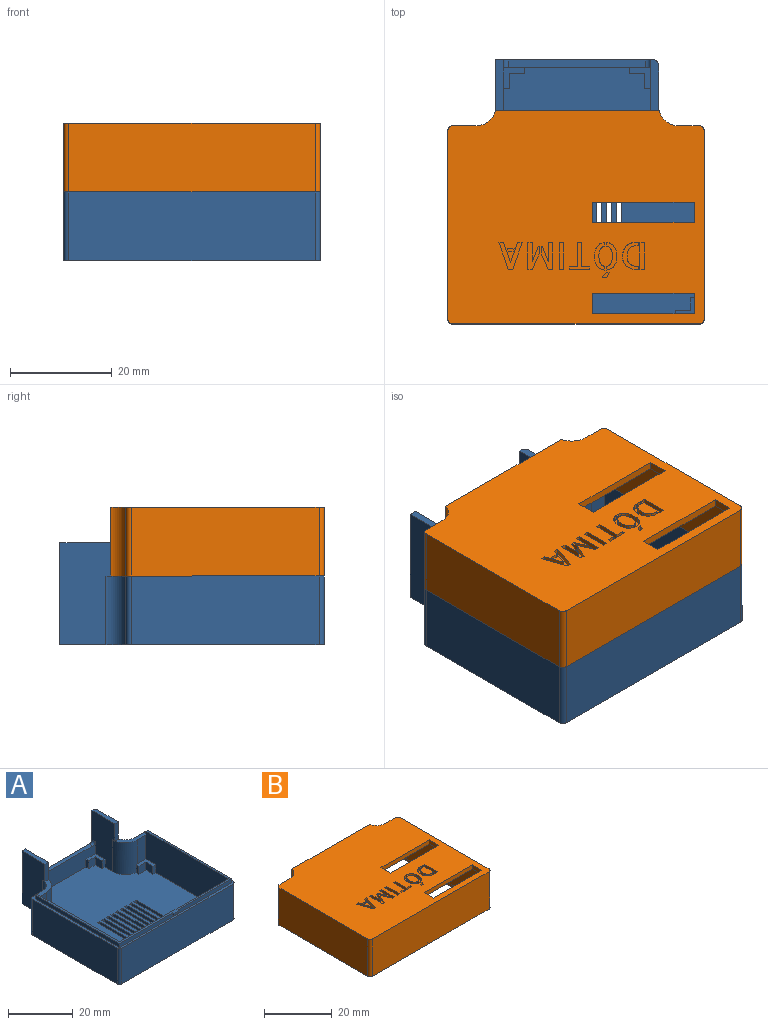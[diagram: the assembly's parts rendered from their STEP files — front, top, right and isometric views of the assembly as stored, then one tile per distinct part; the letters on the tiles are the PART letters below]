
ASSEMBLY  parts=2 mates=1
PART A: 116 faces, bbox 50.5x52x20 mm
  f0: plane 36.75x1.5mm, normal (-1,0,0), area 55.1mm2, adj f1,f5,f14,f115
  f1: plane 49x37.25mm, normal (0,0,1), area 92mm2, adj f0,f4,f5,f9,f25,f26,f110,f112
  f2: cylinder r=5.43mm len=12mm, axis (0,0,-1), area 99.1mm2, adj f7,f8,f11,f14,f66,f70,f101
  f3: cylinder r=5.43mm len=12mm, axis (0,0,-1), area 102.4mm2, adj f6,f8,f14,f27,f78,f98
  f4: plane 36.75x1.5mm, normal (1,0,0), area 55.1mm2, adj f1,f5,f14,f114
  f5: plane 49x1.5mm, normal (0,-1,0), area 71.6mm2, adj f0,f1,f4,f14,f110,f111,f112
  f6: plane 18.5x10mm, normal (-1,0,0), area 149.9mm2, adj f3,f8,f10,f15,f72,f75,f97,f98
  f7: plane 18.5x10mm, normal (1,0,0), area 149.9mm2, adj f2,f8,f10,f15,f92,f96,f100,f101
  f8: plane 49x47.5mm, normal (0,0,1), area 1907.6mm2, adj f2,f3,f6,f7,f9,f10,f25,f26
  f9: plane 36x13.5mm, normal (-1,0,0), area 462.3mm2, adj f1,f8,f26,f27,f77,f81,f83,f86
  f10: plane 29x7.5mm, normal (0,-1,0), area 163.7mm2, adj f6,f7,f8,f28,f73,f75,f95,f96
  f11: plane 12x4.07mm, normal (0,-1,0), area 41.3mm2, adj f2,f13,f14,f25,f65,f66
  f12: plane 52x50.5mm, normal (0,0,-1), area 2256.1mm2, adj f15,f16,f17,f18,f19,f20,f21,f22
  f13: plane 1.57x0.05mm, normal (0,0,1), area 0mm2, adj f11,f25,f65
  f14: plane 50.5x42.93mm, normal (0,0,1), area 127.4mm2, adj f0,f2,f3,f4,f5,f11,f16,f17
  f15: plane 31x20mm, normal (0,1,0), area 272.4mm2, adj f6,f7,f12,f21,f28,f99,f102,f103
  f16: plane 37x13.5mm, normal (1,0,0), area 499.5mm2, adj f12,f14,f108,f109
  f17: plane 48.5x13.5mm, normal (0,-1,0), area 654.8mm2, adj f12,f14,f107,f108
  f18: plane 37x13.5mm, normal (-1,0,0), area 499.5mm2, adj f12,f14,f106,f107
  f19: plane 13.5x4.57mm, normal (0,1,0), area 61.6mm2, adj f12,f14,f20,f106
  f20: cylinder r=3.93mm len=13.5mm, axis (0,0,-1), area 83.4mm2, adj f12,f14,f19,f21
  f21: plane 20x10mm, normal (-1,0,0), area 187.4mm2, adj f12,f14,f15,f20,f100,f102
  f22: plane 20x9mm, normal (1,0,0), area 167.4mm2, adj f12,f14,f23,f97,f99,f105
  f23: cylinder r=3.93mm len=13.5mm, axis (0,0,-1), area 83.4mm2, adj f12,f14,f22,f24
  f24: plane 13.5x4.07mm, normal (0,1,0), area 54.9mm2, adj f12,f14,f23,f109
  f25: plane 36x13.5mm, normal (1,0,0), area 445.9mm2, adj f1,f8,f11,f13,f26,f65,f66,f67
  f26: plane 47.5x13.5mm, normal (0,1,0), area 619mm2, adj f1,f8,f9,f25,f82,f86,f87,f91
  f27: plane 9x3.57mm, normal (0,-1,0), area 32.1mm2, adj f3,f9,f14,f81
  f28: plane 27x1.5mm, normal (0,0,1), area 40.5mm2, adj f10,f15,f103,f104
  f29: plane 15x1.5mm, normal (1,0,0), area 22.5mm2, adj f8,f12,f30,f32
  f30: plane 1.5x1mm, normal (0,-1,0), area 1.5mm2, adj f8,f12,f29,f31
  f31: plane 15x1.5mm, normal (-1,0,0), area 22.5mm2, adj f8,f12,f30,f32
  f32: plane 1.5x1mm, normal (0,1,0), area 1.5mm2, adj f8,f12,f29,f31
  f33: plane 1.5x1mm, normal (0,-1,0), area 1.5mm2, adj f8,f12,f34,f36
  f34: plane 15x1.5mm, normal (-1,0,0), area 22.5mm2, adj f8,f12,f33,f35
  f35: plane 1.5x1mm, normal (0,1,0), area 1.5mm2, adj f8,f12,f34,f36
  f36: plane 15x1.5mm, normal (1,0,0), area 22.5mm2, adj f8,f12,f33,f35
  f37: plane 1.5x1mm, normal (0,-1,0), area 1.5mm2, adj f8,f12,f38,f40
  f38: plane 15x1.5mm, normal (-1,0,0), area 22.5mm2, adj f8,f12,f37,f39
  f39: plane 1.5x1mm, normal (0,1,0), area 1.5mm2, adj f8,f12,f38,f40
  f40: plane 15x1.5mm, normal (1,0,0), area 22.5mm2, adj f8,f12,f37,f39
  f41: plane 1.5x1mm, normal (0,-1,0), area 1.5mm2, adj f8,f12,f42,f44
  f42: plane 15x1.5mm, normal (-1,0,0), area 22.5mm2, adj f8,f12,f41,f43
  f43: plane 1.5x1mm, normal (0,1,0), area 1.5mm2, adj f8,f12,f42,f44
  f44: plane 15x1.5mm, normal (1,0,0), area 22.5mm2, adj f8,f12,f41,f43
  f45: plane 1.5x1mm, normal (0,-1,0), area 1.5mm2, adj f8,f12,f46,f48
  f46: plane 15x1.5mm, normal (-1,0,0), area 22.5mm2, adj f8,f12,f45,f47
  f47: plane 1.5x1mm, normal (0,1,0), area 1.5mm2, adj f8,f12,f46,f48
  f48: plane 15x1.5mm, normal (1,0,0), area 22.5mm2, adj f8,f12,f45,f47
  f49: plane 1.5x1mm, normal (0,-1,0), area 1.5mm2, adj f8,f12,f50,f52
  f50: plane 15x1.5mm, normal (-1,0,0), area 22.5mm2, adj f8,f12,f49,f51
  f51: plane 1.5x1mm, normal (0,1,0), area 1.5mm2, adj f8,f12,f50,f52
  f52: plane 15x1.5mm, normal (1,0,0), area 22.5mm2, adj f8,f12,f49,f51
  f53: plane 15x1.5mm, normal (1,0,0), area 22.5mm2, adj f8,f12,f54,f56
  f54: plane 1.5x1mm, normal (0,-1,0), area 1.5mm2, adj f8,f12,f53,f55
  f55: plane 15x1.5mm, normal (-1,0,0), area 22.5mm2, adj f8,f12,f54,f56
  f56: plane 1.5x1mm, normal (0,1,0), area 1.5mm2, adj f8,f12,f53,f55
  f57: plane 15x1.5mm, normal (1,0,0), area 22.5mm2, adj f8,f12,f58,f60
  f58: plane 1.5x1mm, normal (0,-1,0), area 1.5mm2, adj f8,f12,f57,f59
  f59: plane 15x1.5mm, normal (-1,0,0), area 22.5mm2, adj f8,f12,f58,f60
  f60: plane 1.5x1mm, normal (0,1,0), area 1.5mm2, adj f8,f12,f57,f59
  f61: plane 15x1.5mm, normal (1,0,0), area 22.5mm2, adj f8,f12,f62,f64
  f62: plane 1.5x1mm, normal (0,-1,0), area 1.5mm2, adj f8,f12,f61,f63
  f63: plane 15x1.5mm, normal (-1,0,0), area 22.5mm2, adj f8,f12,f62,f64
  f64: plane 1.5x1mm, normal (0,1,0), area 1.5mm2, adj f8,f12,f61,f63
  f65: plane 3x1.57mm, normal (-0.03,1,0), area 4.7mm2, adj f11,f13,f25,f66
  f66: plane 7.32x5.2mm, normal (0,0,1), area 13.2mm2, adj f2,f11,f25,f65,f67,f68,f69,f70
  f67: plane 3x1.2mm, normal (0,-1,0), area 3.6mm2, adj f8,f25,f66,f68
  f68: plane 6x3mm, normal (1,0,0), area 18mm2, adj f8,f66,f67,f69
  f69: plane 4x3mm, normal (0.03,-1,0), area 12mm2, adj f8,f66,f68,f70
  f70: plane 3x1.2mm, normal (1,0.03,0), area 3.6mm2, adj f2,f8,f66,f69
  f71: plane 3x3mm, normal (-1,0,0), area 9mm2, adj f8,f72,f74,f75
  f72: plane 3x1.2mm, normal (0,-1,0), area 3.6mm2, adj f6,f8,f71,f75
  f73: plane 3x1.2mm, normal (-1,0,0), area 3.6mm2, adj f8,f10,f74,f75
  f74: plane 3x3mm, normal (0,-1,0), area 9mm2, adj f8,f71,f73,f75
  f75: plane 4.2x4.2mm, normal (0,0,1), area 8.6mm2, adj f6,f10,f71,f72,f73,f74
  f76: plane 3x3mm, normal (-1,0,0), area 9mm2, adj f8,f77,f80,f81
  f77: plane 3x1.2mm, normal (0,-1,0), area 3.6mm2, adj f8,f9,f76,f81
  f78: plane 3x0.63mm, normal (0,1,0), area 1.9mm2, adj f3,f8,f79,f81
  f79: plane 3x1.2mm, normal (-1,0,0), area 3.6mm2, adj f8,f78,f80,f81
  f80: plane 3x3mm, normal (0,-1,0), area 9mm2, adj f8,f76,f79,f81
  f81: plane 4.2x4.2mm, normal (0,0,1), area 8.6mm2, adj f9,f27,f76,f77,f78,f79,f80
  f82: plane 3x1.2mm, normal (-1,0,0), area 3.6mm2, adj f8,f26,f85,f86
  f83: plane 3x1.2mm, normal (0,1,0), area 3.6mm2, adj f8,f9,f84,f86
  f84: plane 3x2.5mm, normal (-1,0,0), area 7.5mm2, adj f8,f83,f85,f86
  f85: plane 3x3mm, normal (0,1,0), area 9mm2, adj f8,f82,f84,f86
  f86: plane 4.2x3.7mm, normal (0,0,1), area 8mm2, adj f9,f26,f82,f83,f84,f85
  f87: plane 3x1.2mm, normal (1,0,0), area 3.6mm2, adj f8,f26,f88,f91
  f88: plane 3x2mm, normal (0,1,0), area 6mm2, adj f8,f87,f89,f91
  f89: plane 5x3mm, normal (1,0,0), area 15mm2, adj f8,f88,f90,f91
  f90: plane 3x1.2mm, normal (0,1,0), area 3.6mm2, adj f8,f25,f89,f91
  f91: plane 6.2x3.2mm, normal (0,0,1), area 9.8mm2, adj f25,f26,f87,f88,f89,f90
  f92: plane 3x1.2mm, normal (0,-1,0), area 3.6mm2, adj f7,f8,f93,f96
  f93: plane 3x3mm, normal (1,0,0), area 9mm2, adj f8,f92,f94,f96
  f94: plane 3x3mm, normal (0,-1,0), area 9mm2, adj f8,f93,f95,f96
  f95: plane 3x1.2mm, normal (1,0,0), area 3.6mm2, adj f8,f10,f94,f96
  f96: plane 4.2x4.2mm, normal (0,0,1), area 8.6mm2, adj f7,f10,f92,f93,f94,f95
  f97: plane 6.5x1.5mm, normal (0,-1,0), area 9.8mm2, adj f6,f14,f22,f98,f99
  f98: plane 0.93x0.08mm, normal (0,0,-1), area 0mm2, adj f3,f6,f97
  f99: plane 10x1.5mm, normal (0,0,1), area 14.8mm2, adj f6,f15,f22,f97,f105
  f100: plane 6.5x1.5mm, normal (0,-1,0), area 9.7mm2, adj f7,f14,f21,f101,f102
  f101: plane 0.93x0.08mm, normal (0,0,-1), area 0mm2, adj f2,f7,f100
  f102: plane 10x1.5mm, normal (0,0,1), area 15mm2, adj f7,f15,f21,f100
  f103: cylinder r=1mm len=1.5mm, axis (0,-1,0), area 2.4mm2, adj f6,f10,f15,f28
  f104: cylinder r=1mm len=1.5mm, axis (0,1,0), area 2.4mm2, adj f7,f10,f15,f28
  f105: cylinder r=1mm len=20mm, axis (0,0,-1), area 31.4mm2, adj f12,f15,f22,f99
  f106: cylinder r=1mm len=13.5mm, axis (0,0,1), area 21.2mm2, adj f12,f14,f18,f19
  f107: cylinder r=1mm len=13.5mm, axis (0,0,-1), area 21.2mm2, adj f12,f14,f17,f18
  f108: cylinder r=1mm len=13.5mm, axis (0,0,1), area 21.2mm2, adj f12,f14,f16,f17
  f109: cylinder r=1mm len=13.5mm, axis (0,0,-1), area 21.2mm2, adj f12,f14,f16,f24
  f110: plane 0.75x0.5mm, normal (-1,0,0), area 0.4mm2, adj f1,f5,f111,f113
  f111: plane 2.5x0.5mm, normal (0,0,-1), area 1.3mm2, adj f5,f110,f112,f113
  f112: plane 0.75x0.5mm, normal (1,0,0), area 0.4mm2, adj f1,f5,f111,f113
  f113: plane 2.5x0.75mm, normal (0,-1,0), area 1.9mm2, adj f1,f110,f111,f112
  f114: plane 1.5x0.75mm, normal (0,1,0), area 1.1mm2, adj f1,f4,f9,f14
  f115: plane 1.5x0.75mm, normal (0,1,0), area 1.1mm2, adj f0,f1,f14,f25
PART B: 160 faces, bbox 50.5x42x13.5 mm
  f0: plane 1.5x0.75mm, normal (0,-1,0), area 1.1mm2, adj f1,f4,f17,f159
  f1: plane 49x38mm, normal (0,0,-1), area 93.1mm2, adj f0,f2,f15,f16,f17,f18,f19,f20
  f2: plane 49x1.5mm, normal (0,1,0), area 71.6mm2, adj f1,f4,f15,f17,f154,f155,f156
  f3: plane 50.5x42mm, normal (0,0,1), area 1854.2mm2, adj f5,f9,f10,f11,f12,f13,f14,f23
  f4: plane 50.5x42mm, normal (0,0,-1), area 126.2mm2, adj f0,f2,f5,f7,f8,f9,f10,f11
  f5: cylinder r=3.93mm len=13.5mm, axis (0,0,-1), area 70.7mm2, adj f3,f4,f9,f23
  f6: plane 47.5x38.5mm, normal (0,0,-1), area 1633.5mm2, adj f7,f8,f18,f19,f20,f21,f22,f24
  f7: cylinder r=5.43mm len=12mm, axis (0,0,-1), area 77.1mm2, adj f4,f6,f21,f23,f24,f25
  f8: cylinder r=5.43mm len=12mm, axis (0,0,-1), area 77.1mm2, adj f4,f6,f22,f23,f24,f25
  f9: plane 13.5x4.07mm, normal (0,1,0), area 54.9mm2, adj f3,f4,f5,f153
  f10: cylinder r=3.93mm len=13.5mm, axis (0,0,-1), area 70.7mm2, adj f3,f4,f11,f23
  f11: plane 13.5x4.57mm, normal (0,1,0), area 61.6mm2, adj f3,f4,f10,f150
  f12: plane 37x13.5mm, normal (-1,0,0), area 499.5mm2, adj f3,f4,f150,f151
  f13: plane 48.5x13.5mm, normal (0,-1,0), area 654.8mm2, adj f3,f4,f151,f152
  f14: plane 37x13.5mm, normal (1,0,0), area 499.5mm2, adj f3,f4,f152,f153
  f15: plane 37.5x1.5mm, normal (1,0,0), area 56.2mm2, adj f1,f2,f4,f16
  f16: plane 1.5x0.75mm, normal (0,-1,0), area 1.1mm2, adj f1,f4,f15,f158
  f17: plane 37.5x1.5mm, normal (-1,0,0), area 56.2mm2, adj f0,f1,f2,f4
  f18: plane 36x10.5mm, normal (-1,0,0), area 378mm2, adj f1,f6,f19,f22
  f19: plane 47.5x10.5mm, normal (0,1,0), area 498.8mm2, adj f1,f6,f18,f20
  f20: plane 36x10.5mm, normal (1,0,0), area 378mm2, adj f1,f6,f19,f21
  f21: plane 12x4.07mm, normal (0,-1,0), area 48.8mm2, adj f4,f6,f7,f20,f158
  f22: plane 12x3.57mm, normal (0,-1,0), area 42.8mm2, adj f4,f6,f8,f18,f159
  f23: plane 32.23x13.5mm, normal (0,1,0), area 274.6mm2, adj f3,f4,f5,f7,f8,f10,f25
  f24: plane 30.72x6.5mm, normal (0,-1,0), area 199.7mm2, adj f6,f7,f8,f25
  f25: plane 30.72x2mm, normal (0,0,-1), area 59.6mm2, adj f7,f8,f23,f24
  f26: plane 20x1.5mm, normal (0,1,0), area 30mm2, adj f3,f6,f27,f29
  f27: plane 4x1.5mm, normal (-1,0,0), area 6mm2, adj f3,f6,f26,f28
  f28: plane 20x1.5mm, normal (0,-1,0), area 30mm2, adj f3,f6,f27,f29
  f29: plane 4x1.5mm, normal (1,0,0), area 6mm2, adj f3,f6,f26,f28
  f30: plane 20x1.5mm, normal (0,1,0), area 30mm2, adj f3,f6,f31,f33
  f31: plane 4x1.5mm, normal (-1,0,0), area 6mm2, adj f3,f6,f30,f32
  f32: plane 20x1.5mm, normal (0,-1,0), area 30mm2, adj f3,f6,f31,f33
  f33: plane 4x1.5mm, normal (1,0,0), area 6mm2, adj f3,f6,f30,f32
  f34: plane 1x0.89mm, normal (0,-1,0), area 0.9mm2, adj f3,f35,f40,f41
  f35: plane 5.3x1.84mm, normal (0.94,0.33,0), area 5.6mm2, adj f3,f34,f36,f41
  f36: plane 1x0.86mm, normal (0,1,0), area 0.9mm2, adj f3,f35,f37,f41
  f37: plane 5.3x1.86mm, normal (-0.94,0.33,0), area 5.6mm2, adj f3,f36,f38,f41
  f38: plane 1x0.9mm, normal (0,-1,0), area 0.9mm2, adj f3,f37,f39,f41
  f39: plane 3.97x1.39mm, normal (0.94,-0.33,0), area 4.2mm2, adj f3,f38,f40,f41
  f40: plane 3.97x1.38mm, normal (-0.95,-0.33,0), area 4.2mm2, adj f3,f34,f39,f41
  f41: plane 5.3x4.56mm, normal (0,0,1), area 8.9mm2, adj f34,f35,f36,f37,f38,f39,f40
  f42: plane 1x0.58mm, normal (0.94,0.34,0), area 0.6mm2, adj f3,f43,f45,f46
  f43: plane 1x0.97mm, normal (0,1,0), area 1mm2, adj f3,f42,f44,f46
  f44: plane 1x0.58mm, normal (-0.95,0.33,0), area 0.6mm2, adj f3,f43,f45,f46
  f45: plane 1.38x1mm, normal (0,-1,0), area 1.4mm2, adj f3,f42,f44,f46
  f46: plane 1.38x0.58mm, normal (0,0,1), area 0.7mm2, adj f42,f43,f44,f45
  f47: plane 1x0.88mm, normal (0,1,0), area 0.9mm2, adj f3,f48,f54,f55
  f48: plane 3.29x1.43mm, normal (-0.92,0.4,0), area 3.6mm2, adj f3,f47,f49,f55
  f49: plane 1.32x1mm, normal (-1,0,0), area 1.3mm2, adj f3,f48,f50,f55
  f50: plane 1x0.24mm, normal (0,-1,0), area 0.2mm2, adj f3,f49,f51,f55
  f51: plane 2.95x1.19mm, normal (0.93,-0.37,0), area 3.2mm2, adj f3,f50,f52,f55
  f52: plane 3.65x1mm, normal (-1,0,0), area 3.7mm2, adj f3,f51,f53,f55
  f53: plane 1x0.88mm, normal (0,-1,0), area 0.9mm2, adj f3,f52,f54,f55
  f54: plane 5.31x1mm, normal (1,0,0), area 5.3mm2, adj f3,f47,f53,f55
  f55: plane 5.31x2.3mm, normal (0,0,1), area 7.1mm2, adj f47,f48,f49,f50,f51,f52,f53,f54
  f56: plane 1x0.88mm, normal (0,1,0), area 0.9mm2, adj f3,f57,f63,f64
  f57: plane 5.31x1mm, normal (-1,0,0), area 5.3mm2, adj f3,f56,f58,f64
  f58: plane 1x0.88mm, normal (0,-1,0), area 0.9mm2, adj f3,f57,f59,f64
  f59: plane 3.65x1mm, normal (1,0,0), area 3.7mm2, adj f3,f58,f60,f64
  f60: plane 2.95x1.19mm, normal (-0.93,-0.38,0), area 3.2mm2, adj f3,f59,f61,f64
  f61: plane 1x0.23mm, normal (0,-1,0), area 0.2mm2, adj f3,f60,f62,f64
  f62: plane 1.33x1mm, normal (1,0,0), area 1.3mm2, adj f3,f61,f63,f64
  f63: plane 3.28x1.43mm, normal (0.92,0.4,0), area 3.6mm2, adj f3,f56,f62,f64
  f64: plane 5.31x2.3mm, normal (0,0,1), area 7.1mm2, adj f56,f57,f58,f59,f60,f61,f62,f63
  f65: plane 1x0.88mm, normal (0,-1,0), area 0.9mm2, adj f3,f66,f68,f69
  f66: plane 5.31x1mm, normal (1,0,0), area 5.3mm2, adj f3,f65,f67,f69
  f67: plane 1x0.88mm, normal (0,1,0), area 0.9mm2, adj f3,f66,f68,f69
  f68: plane 5.31x1mm, normal (-1,0,0), area 5.3mm2, adj f3,f65,f67,f69
  f69: plane 5.31x0.88mm, normal (0,0,1), area 4.7mm2, adj f65,f66,f67,f68
  f70: plane 1x0.59mm, normal (1,0,0), area 0.6mm2, adj f3,f71,f77,f78
  f71: plane 4.04x1mm, normal (0,1,0), area 4mm2, adj f3,f70,f72,f78
  f72: plane 1x0.59mm, normal (-1,0,0), area 0.6mm2, adj f3,f71,f73,f78
  f73: plane 1.58x1mm, normal (0,-1,0), area 1.6mm2, adj f3,f72,f74,f78
  f74: plane 4.72x1mm, normal (-1,0,0), area 4.7mm2, adj f3,f73,f75,f78
  f75: plane 1x0.87mm, normal (0,-1,0), area 0.9mm2, adj f3,f74,f76,f78
  f76: plane 4.72x1mm, normal (1,0,0), area 4.7mm2, adj f3,f75,f77,f78
  f77: plane 1.58x1mm, normal (0,-1,0), area 1.6mm2, adj f3,f70,f76,f78
  f78: plane 5.31x4.04mm, normal (0,0,1), area 6.5mm2, adj f70,f71,f72,f73,f74,f75,f76,f77
  f79: extruded ~1.18x1mm, area 1.2mm2, adj f3,f80,f100,f101
  f80: plane 1x0.44mm, normal (0,1,0), area 0.4mm2, adj f3,f79,f81,f101
  f81: plane 1x0.65mm, normal (-1,0,0), area 0.7mm2, adj f3,f80,f82,f101
  f82: plane 1x0.21mm, normal (0,-1,0), area 0.2mm2, adj f3,f81,f83,f101
  f83: extruded ~1.01x1mm, area 1mm2, adj f3,f82,f84,f101
  f84: extruded ~1x0.62mm, area 0.8mm2, adj f3,f83,f85,f101
  f85: extruded ~1x0.59mm, area 0.7mm2, adj f3,f84,f86,f101
  f86: extruded ~1x0.66mm, area 0.7mm2, adj f3,f85,f87,f101
  f87: extruded ~1.63x1mm, area 1.7mm2, adj f3,f86,f88,f101
  f88: extruded ~1.27x1mm, area 1.4mm2, adj f3,f87,f89,f101
  f89: plane 1x0.56mm, normal (0,1,0), area 0.6mm2, adj f3,f88,f90,f101
  f90: plane 1x0.63mm, normal (-1,0,0), area 0.6mm2, adj f3,f89,f91,f101
  f91: plane 1x0.85mm, normal (0,-1,0), area 0.9mm2, adj f3,f90,f92,f101
  f92: extruded ~1x0.31mm, area 0.3mm2, adj f3,f91,f93,f101
  f93: extruded ~1x0.46mm, area 0.5mm2, adj f3,f92,f94,f101
  f94: extruded ~1x0.52mm, area 0.6mm2, adj f3,f93,f95,f101
  f95: extruded ~1x0.49mm, area 0.7mm2, adj f3,f94,f96,f101
  f96: extruded ~1x0.78mm, area 0.9mm2, adj f3,f95,f97,f101
  f97: extruded ~1.12x1mm, area 1.1mm2, adj f3,f96,f98,f101
  f98: extruded ~1x0.93mm, area 0.9mm2, adj f3,f97,f99,f101
  f99: extruded ~1x0.8mm, area 1mm2, adj f3,f98,f100,f101
  f100: extruded ~1x0.84mm, area 1mm2, adj f3,f79,f99,f101
  f101: plane 5.31x3.13mm, normal (0,0,1), area 6.3mm2, adj f79,f80,f81,f82,f83,f84,f85,f86
  f102: extruded ~1.13x1mm, area 1.1mm2, adj f3,f103,f119,f120
  f103: extruded ~1.14x1mm, area 1.2mm2, adj f3,f102,f104,f120
  f104: extruded ~1x0.84mm, area 0.9mm2, adj f3,f103,f105,f120
  f105: extruded ~1x0.66mm, area 0.8mm2, adj f3,f104,f106,f120
  f106: extruded ~1x0.82mm, area 0.9mm2, adj f3,f105,f107,f120
  f107: plane 1x0.71mm, normal (1,0,0), area 0.7mm2, adj f3,f106,f108,f120
  f108: extruded ~1x0.45mm, area 0.5mm2, adj f3,f107,f109,f120
  f109: extruded ~1x0.38mm, area 0.5mm2, adj f3,f108,f110,f120
  f110: extruded ~1x0.61mm, area 0.7mm2, adj f3,f109,f111,f120
  f111: extruded ~1x0.88mm, area 0.9mm2, adj f3,f110,f112,f120
  f112: extruded ~1x0.87mm, area 0.9mm2, adj f3,f111,f113,f120
  f113: extruded ~1x0.61mm, area 0.7mm2, adj f3,f112,f114,f120
  f114: extruded ~1x0.37mm, area 0.5mm2, adj f3,f113,f115,f120
  f115: extruded ~1x0.46mm, area 0.5mm2, adj f3,f114,f116,f120
  f116: plane 1x0.72mm, normal (1,0,0), area 0.7mm2, adj f3,f115,f117,f120
  f117: extruded ~1x0.82mm, area 0.9mm2, adj f3,f116,f118,f120
  f118: extruded ~1x0.66mm, area 0.8mm2, adj f3,f117,f119,f120
  f119: extruded ~1x0.84mm, area 0.9mm2, adj f3,f102,f118,f120
  f120: plane 5.42x2.07mm, normal (0,0,1), area 5.2mm2, adj f102,f103,f104,f105,f106,f107,f108,f109
  f121: extruded ~1x0.82mm, area 0.8mm2, adj f3,f122,f138,f139
  f122: plane 1x0.71mm, normal (-1,0,0), area 0.7mm2, adj f3,f121,f123,f139
  f123: extruded ~1x0.45mm, area 0.5mm2, adj f3,f122,f124,f139
  f124: extruded ~1x0.38mm, area 0.5mm2, adj f3,f123,f125,f139
  f125: extruded ~1x0.61mm, area 0.7mm2, adj f3,f124,f126,f139
  f126: extruded ~1x0.88mm, area 0.9mm2, adj f3,f125,f127,f139
  f127: extruded ~1x0.88mm, area 0.9mm2, adj f3,f126,f128,f139
  f128: extruded ~1x0.61mm, area 0.7mm2, adj f3,f127,f129,f139
  f129: extruded ~1x0.37mm, area 0.5mm2, adj f3,f128,f130,f139
  f130: extruded ~1x0.46mm, area 0.5mm2, adj f3,f129,f131,f139
  f131: plane 1x0.71mm, normal (-1,0,0), area 0.7mm2, adj f3,f130,f132,f139
  f132: extruded ~1x0.82mm, area 0.9mm2, adj f3,f131,f133,f139
  f133: extruded ~1x0.65mm, area 0.8mm2, adj f3,f132,f134,f139
  f134: extruded ~1x0.84mm, area 1mm2, adj f3,f133,f135,f139
  f135: extruded ~1.14x1mm, area 1.2mm2, adj f3,f134,f136,f139
  f136: extruded ~1.13x1mm, area 1.1mm2, adj f3,f135,f137,f139
  f137: extruded ~1x0.84mm, area 0.9mm2, adj f3,f136,f138,f139
  f138: extruded ~1x0.66mm, area 0.8mm2, adj f3,f121,f137,f139
  f139: plane 5.42x2.07mm, normal (0,0,1), area 5.2mm2, adj f121,f122,f123,f124,f125,f126,f127,f128
  f140: plane 1.02x1mm, normal (0.79,-0.61,0), area 1.3mm2, adj f3,f141,f143,f144
  f141: plane 1x0.88mm, normal (0,1,0), area 0.9mm2, adj f3,f140,f142,f144
  f142: plane 1.02x1mm, normal (-0.9,0.43,0), area 1.1mm2, adj f3,f141,f143,f144
  f143: plane 1x0.58mm, normal (0,-1,0), area 0.6mm2, adj f3,f140,f142,f144
  f144: plane 1.36x1.02mm, normal (0,0,1), area 0.7mm2, adj f140,f141,f142,f143
  f145: plane 1x0.86mm, normal (0,1,0), area 0.9mm2, adj f3,f146,f148,f149
  f146: plane 5.31x1mm, normal (-1,0,0), area 5.3mm2, adj f3,f145,f147,f149
  f147: plane 1x0.86mm, normal (0,-1,0), area 0.9mm2, adj f3,f146,f148,f149
  f148: plane 5.31x1mm, normal (1,0,0), area 5.3mm2, adj f3,f145,f147,f149
  f149: plane 5.31x0.86mm, normal (0,0,1), area 4.6mm2, adj f145,f146,f147,f148
  f150: cylinder r=1mm len=13.5mm, axis (0,0,1), area 21.2mm2, adj f3,f4,f11,f12
  f151: cylinder r=1mm len=13.5mm, axis (0,0,-1), area 21.2mm2, adj f3,f4,f12,f13
  f152: cylinder r=1mm len=13.5mm, axis (0,0,1), area 21.2mm2, adj f3,f4,f13,f14
  f153: cylinder r=1mm len=13.5mm, axis (0,0,-1), area 21.2mm2, adj f3,f4,f9,f14
  f154: plane 0.75x0.5mm, normal (-1,0,0), area 0.4mm2, adj f1,f2,f155,f157
  f155: plane 2.5x0.5mm, normal (0,0,1), area 1.3mm2, adj f2,f154,f156,f157
  f156: plane 0.75x0.5mm, normal (1,0,0), area 0.4mm2, adj f1,f2,f155,f157
  f157: plane 2.5x0.75mm, normal (0,1,0), area 1.9mm2, adj f1,f154,f155,f156
  f158: plane 1.5x0.75mm, normal (-1,0,0), area 1.1mm2, adj f1,f4,f16,f21
  f159: plane 1.5x0.75mm, normal (1,0,0), area 1.1mm2, adj f0,f1,f4,f22
PLACE A t=(-49.49,-12.32,-1.38)mm fixed
PLACE B t=(-49.49,-12.32,-1.38)mm
MATE slider B.f1 <-> A.f1  axis (0,0,-1) through (-24.24,-38.57,0.12)mm
